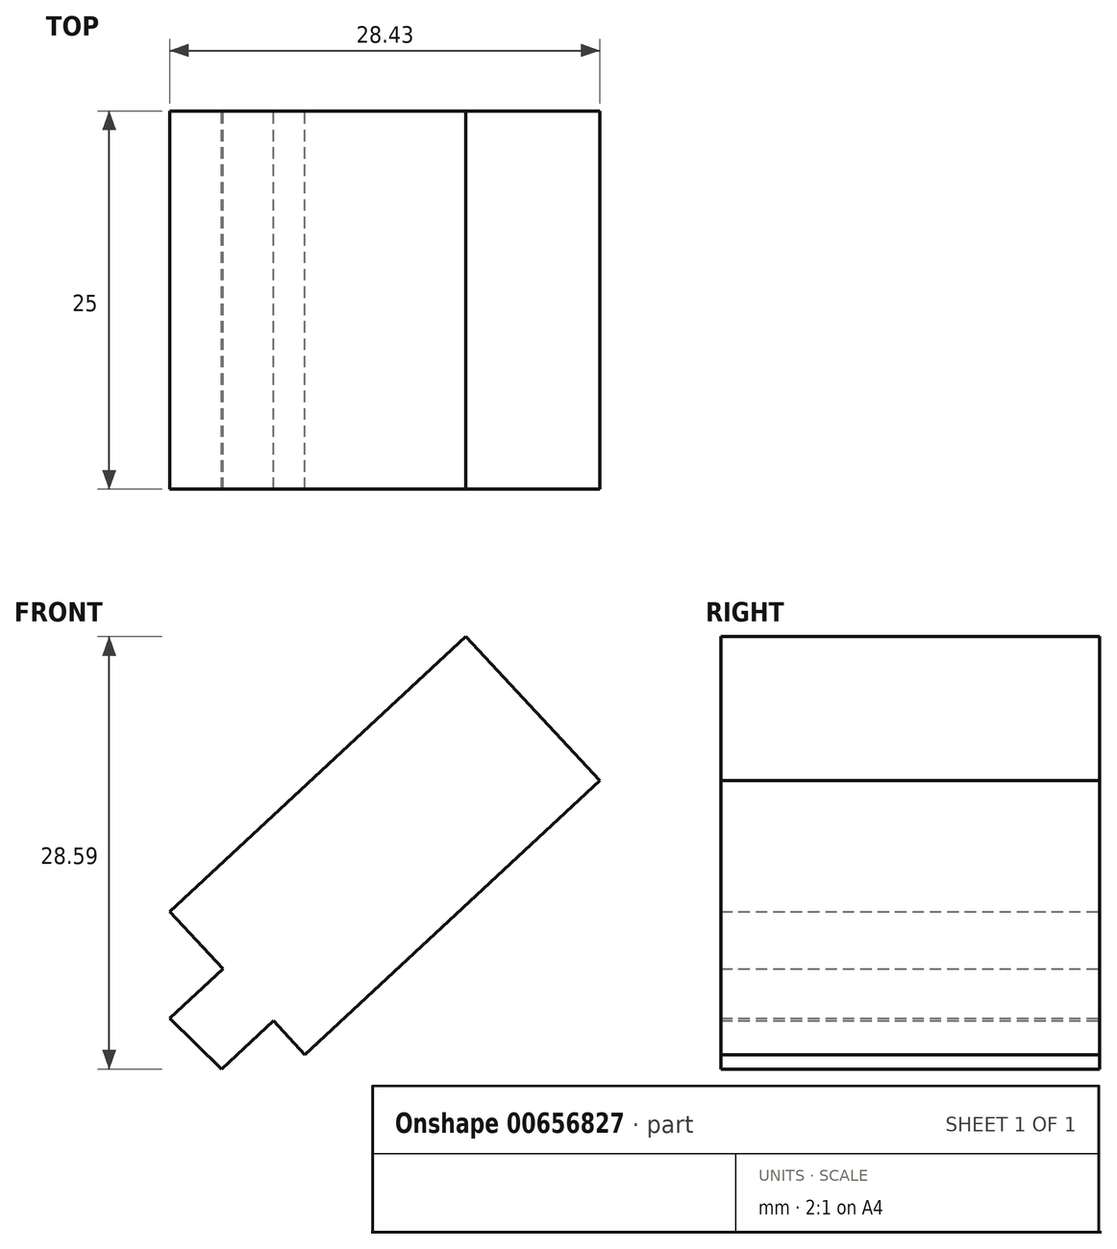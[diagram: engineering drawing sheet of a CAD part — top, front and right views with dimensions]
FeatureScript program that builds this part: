
annotation { "Feature Type Name" : "Feature", "Feature Type Description" : "" }
export const myFeature = defineFeature(function(context is Context, id is Id, definition is map)
    precondition{}
    {
        {
            var Q0;
            Q0=qCreatedBy(makeId("Front.planeOp"),FACE);
            var sketch = newSketch(context, id + "F0", { "sketchPlane" : qUnion([Q0])});
            skLineSegment(sketch, "E0", {"start": v(43.59, 33.99) * mm, "end": v(24.01, 15.8) * mm});
            skLineSegment(sketch, "E1", {"start": v(43.59, 33.99) * mm, "end": v(52.44, 24.47) * mm});
            skLineSegment(sketch, "E2", {"start": v(52.44, 24.47) * mm, "end": v(32.95, 6.35) * mm});
            skLineSegment(sketch, "E3", {"start": v(32.95, 6.35) * mm, "end": v(30.87, 8.58) * mm});
            skLineSegment(sketch, "E4", {"start": v(30.87, 8.58) * mm, "end": v(27.45, 5.4) * mm});
            skLineSegment(sketch, "E5", {"start": v(24.01, 15.8) * mm, "end": v(27.53, 12.01) * mm});
            skLineSegment(sketch, "E6", {"start": v(27.53, 12.01) * mm, "end": v(24.01, 8.74) * mm});
            skLineSegment(sketch, "E7.bottom", {"start": v(24.74, 5.69) * mm, "end": v(20.54, 5.69) * mm});
            skLineSegment(sketch, "E7.top", {"start": v(24.74, -6.64) * mm, "end": v(20.54, -6.64) * mm});
            skLineSegment(sketch, "E7.left", {"start": v(24.74, 5.69) * mm, "end": v(24.74, -6.64) * mm});
            skLineSegment(sketch, "E7.right", {"start": v(20.54, 5.69) * mm, "end": v(20.54, -6.64) * mm});
            skLineSegment(sketch, "E8", {"start": v(24.01, 8.74) * mm, "end": v(27.45, 5.4) * mm});
            skSolve(sketch);
        }
        {
            var Q0;
            Q0=makeQuery(id+"F0.imprint","IMPRINT",FACE,{"disambiguationData":[TD([[makeQuery(id+"F0.imprint","IMPRINT",EDGE,{"derivedFrom":sQuery(id+"F0.wireOp",EDGE,"E7.bottom")}),1.0]])]});
            var Q1;
            Q1=makeQuery(id+"F0.imprint","IMPRINT",FACE,{"disambiguationData":[TD([[makeQuery(id+"F0.imprint","IMPRINT",EDGE,{"derivedFrom":sQuery(id+"F0.wireOp",EDGE,"E0")}),1.0]])]});
            extrude(context, id + "F1", {"entities" : qUnion([Q0, Q1]), "depth" : 25 * mm, "offsetDistance" : 25 * mm});
        }
        {
            var Q0;
            Q0=makeQuery(id+"F1.opExtrude","SWEPT_BODY",BODY,{"disambiguationData":[OSD([sQuery(id+"F0.wireOp",EDGE,"E7.bottom"),sQuery(id+"F0.wireOp",EDGE,"E7.top"),sQuery(id+"F0.wireOp",EDGE,"E7.left"),sQuery(id+"F0.wireOp",EDGE,"E7.right")])]});
            deleteBodies(context, id + "F2", {"entities" : qUnion([Q0])});
        }
    });
